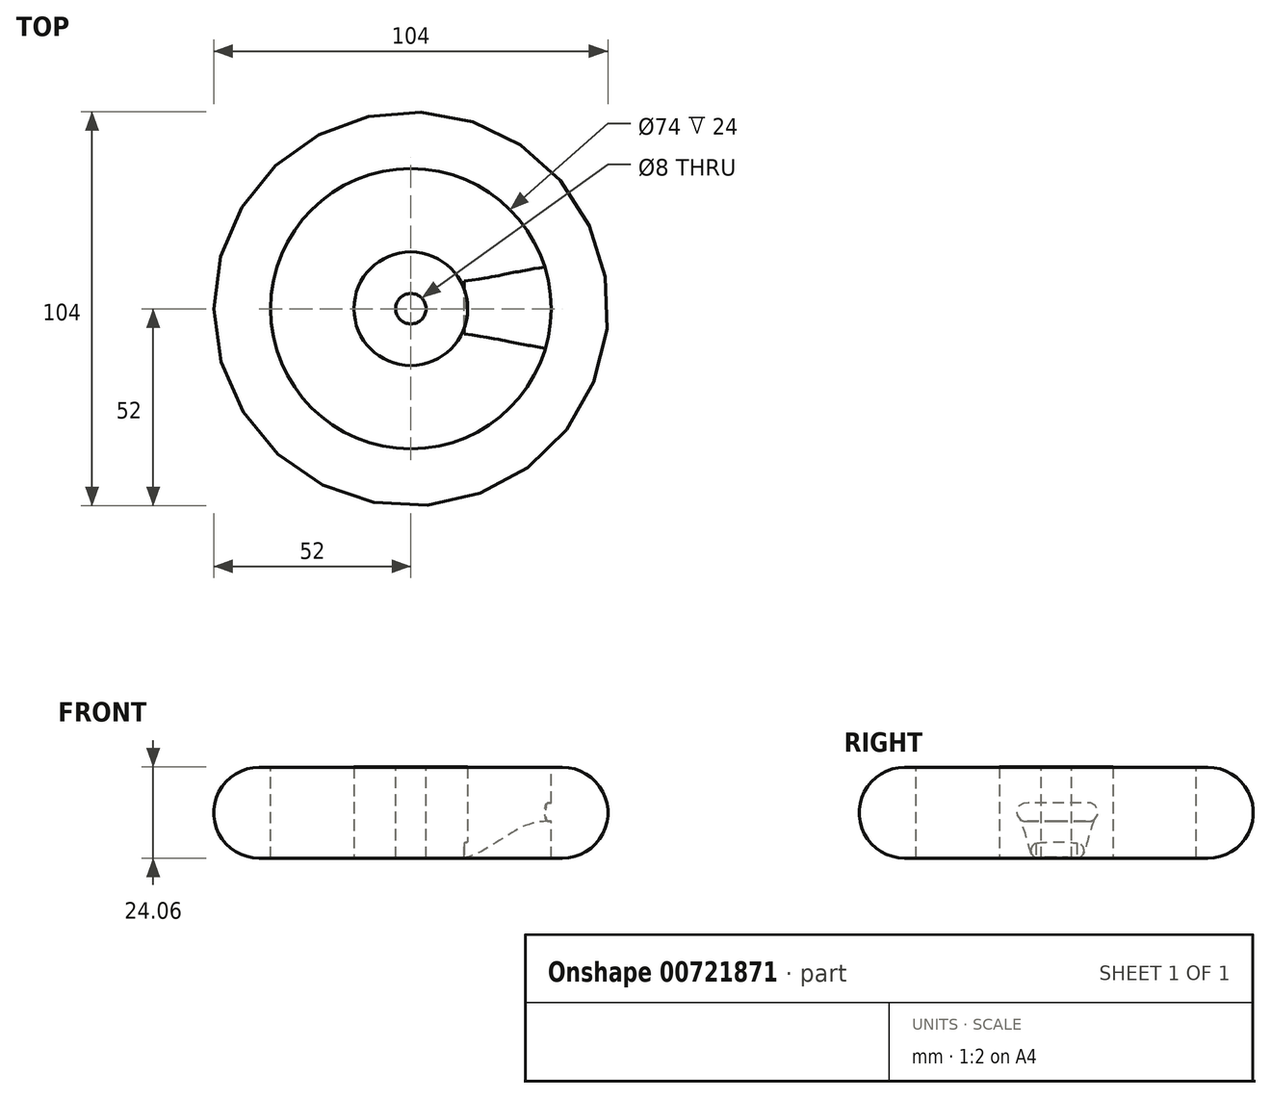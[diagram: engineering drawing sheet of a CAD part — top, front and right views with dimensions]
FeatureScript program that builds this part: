
annotation { "Feature Type Name" : "Feature", "Feature Type Description" : "" }
export const myFeature = defineFeature(function(context is Context, id is Id, definition is map)
    precondition{}
    {
        {
            var Q0;
            Q0=qCreatedBy(makeId("Top.planeOp"),FACE);
            var sketch = newSketch(context, id + "F0", { "sketchPlane" : qUnion([Q0])});
            skCircle(sketch, "E0", {"center": v(0, 0) * mm, "radius": 40 * mm});
            skSolve(sketch);
        }
        {
            var Q0;
            Q0=qCreatedBy(makeId("Front.planeOp"),FACE);
            var sketch = newSketch(context, id + "F1", { "sketchPlane" : qUnion([Q0])});
            skArc(sketch, "E1", {"start": v(-40, 12) * mm, "mid": v(-52, 0) * mm, "end": v(-40, -12) * mm});
            skLineSegment(sketch, "E2", {"start": v(-40, 12) * mm, "end": v(-37, 12) * mm});
            skLineSegment(sketch, "E3", {"start": v(-40, -12) * mm, "end": v(-37, -12) * mm});
            skLineSegment(sketch, "E4", {"start": v(-37, -12) * mm, "end": v(-37, 12) * mm});
            skSolve(sketch);
        }
        {
            var Q0;
            Q0=makeQuery(id+"F1.imprint","IMPRINT",FACE,{"disambiguationData":[TD([[makeQuery(id+"F1.imprint","IMPRINT",EDGE,{"derivedFrom":sQuery(id+"F1.wireOp",EDGE,"E1")}),1.0]])]});
            var Q1;
            Q1=sQuery(id+"F0.wireOp",EDGE,"E0");
            sweep(context, id + "F2", {"profiles" : qUnion([Q0]), "path" : qUnion([Q1])});
        }
        {
            var Q0;
            Q0=qCreatedBy(makeId("Right.planeOp"),FACE);
            cPlane(context, id + "F3", {"entities" : qUnion([Q0]), "cplaneType" : CPlaneType.OFFSET, "offset" : 40 * mm, "width" : 150 * mm, "height" : 150 * mm});
        }
        {
            var Q0;
            Q0=qCreatedBy(id+"F3.planeOp",FACE);
            var sketch = newSketch(context, id + "F4", { "sketchPlane" : qUnion([Q0])});
            skLineSegment(sketch, "E5", {"start": v(-8.69, 0) * mm, "end": v(9.31, 0) * mm});
            skArc(sketch, "E6.0.startCap", {"start": v(-8.69, -2.5) * mm, "mid": v(-11.19, 0) * mm, "end": v(-8.69, 2.5) * mm});
            skArc(sketch, "E6.0.endCap", {"start": v(9.31, 2.5) * mm, "mid": v(11.81, 0) * mm, "end": v(9.31, -2.5) * mm});
            skLineSegment(sketch, "E6.0.left", {"start": v(-8.69, 2.5) * mm, "end": v(9.31, 2.5) * mm});
            skLineSegment(sketch, "E6.0.right", {"start": v(-8.69, -2.5) * mm, "end": v(9.31, -2.5) * mm});
            skSolve(sketch);
        }
        {
            var Q0;
            Q0=qCreatedBy(makeId("Right.planeOp"),FACE);
            cPlane(context, id + "F5", {"entities" : qUnion([Q0]), "cplaneType" : CPlaneType.OFFSET, "offset" : 14 * mm, "width" : 150 * mm, "height" : 150 * mm});
        }
        {
            var Q0;
            Q0=qCreatedBy(id+"F5.planeOp",FACE);
            var sketch = newSketch(context, id + "F6", { "sketchPlane" : qUnion([Q0])});
            skLineSegment(sketch, "E7", {"start": v(-4.69, -10) * mm, "end": v(5.31, -10) * mm});
            skArc(sketch, "E8.0.startCap", {"start": v(-4.69, -12) * mm, "mid": v(-6.69, -10) * mm, "end": v(-4.69, -8) * mm});
            skArc(sketch, "E8.0.endCap", {"start": v(5.31, -8) * mm, "mid": v(7.31, -10) * mm, "end": v(5.31, -12) * mm});
            skLineSegment(sketch, "E8.0.left", {"start": v(-4.69, -8) * mm, "end": v(5.31, -8) * mm});
            skLineSegment(sketch, "E8.0.right", {"start": v(-4.69, -12) * mm, "end": v(5.31, -12) * mm});
            skSolve(sketch);
        }
        {
            var Q0;
            Q0=qCreatedBy(makeId("Front.planeOp"),FACE);
            var sketch = newSketch(context, id + "F7", { "sketchPlane" : qUnion([Q0])});
            skFitSpline(sketch, "E9", {"points": [v(14, -12) * mm, v(21.22, -8.7) * mm, v(25.51, -5.98) * mm, v(29.9, -3.56) * mm, v(34.75, -2.35) * mm, v(40, -2.5) * mm], "startDerivative": vector(34.97, 7.52) * mm, "endDerivative": vector(31.17, -2.37) * mm});
            skSolve(sketch);
        }
        {
            var Q1;
            Q1 = qSketchRegion(id + "F4", true);
            var Q2;
            Q2 = qSketchRegion(id + "F6", true);
            var Q3;
            Q3 = qConstructionFilter(qBodyType(qCreatedBy(id + "F7" ,EDGE), BodyType.WIRE), ConstructionObject.NO);
            loft(context, id + "F8", {"operationType" : NewBodyOperationType.ADD, "addGuides" : true, "sheetProfilesArray" : [{ "sheetProfileEntities" : qUnion([Q1]) }, { "sheetProfileEntities" : qUnion([Q2]) }], "guidesArray" : [{ "guideEntities" : qUnion([Q3]), "guideDerivativeType" : LoftGuideDerivativeType.DEFAULT, "guideDerivativeMagnitude" : 1 }]});
        }
        {
            var Q0;
            Q0=qCreatedBy(makeId("Front.planeOp"),FACE);
            var sketch = newSketch(context, id + "F9", { "sketchPlane" : qUnion([Q0])});
            skLineSegment(sketch, "E10.bottom", {"start": v(0, -11.94) * mm, "end": v(15, -11.94) * mm});
            skLineSegment(sketch, "E10.top", {"start": v(0, 12.06) * mm, "end": v(15, 12.06) * mm});
            skLineSegment(sketch, "E10.left", {"start": v(0, -11.94) * mm, "end": v(0, 12.06) * mm});
            skLineSegment(sketch, "E10.right", {"start": v(15, -11.94) * mm, "end": v(15, 12.06) * mm});
            skSolve(sketch);
        }
        {
            var Q0;
            Q0=makeQuery(id+"F9.imprint","IMPRINT",FACE,{"disambiguationData":[TD([[makeQuery(id+"F9.imprint","IMPRINT",EDGE,{"derivedFrom":sQuery(id+"F9.wireOp",EDGE,"E10.bottom")}),1.0]])]});
            var Q1;
            Q1=sQuery(id+"F9.wireOp",EDGE,"E10.left");
            revolve(context, id + "F10", {"operationType" : NewBodyOperationType.ADD, "surfaceOperationType" : NewSurfaceOperationType.NEW, "entities" : qUnion([Q0]), "axis" : qUnion([Q1]), "revolveType" : RevolveType.FULL});
        }
        {
            var Q0;
            Q0=makeQuery(id+"F10.opRevolve","SWEPT_FACE",FACE,{"disambiguationData":[OSD([sQuery(id+"F9.wireOp",EDGE,"E10.top")])]});
            var sketch = newSketch(context, id + "F11", { "sketchPlane" : qUnion([Q0])});
            skPoint(sketch, "E11", {"position": v(0, 0) * mm});
            skSolve(sketch);
        }
        {
            var Q0;
            Q0=sQuery(id+"F11.wireOp",VERTEX,"E11");
            var Q1;
            Q1=makeQuery(id+"F2.opSweep","SWEPT_BODY",BODY,{"disambiguationData":[OSD([sQuery(id+"F0.wireOp",EDGE,"E0"),sQuery(id+"F1.wireOp",EDGE,"E1"),sQuery(id+"F1.wireOp",EDGE,"E2"),sQuery(id+"F1.wireOp",EDGE,"E3"),sQuery(id+"F1.wireOp",EDGE,"E4")])]});
            hole(context, id + "F12", {"style" : HoleStyle.SIMPLE, "endStyle" : HoleEndStyle.BLIND, "holeDiameter" : 8 * mm, "majorDiameter" : 5 * mm, "holeDepth" : 50 * mm, "isTappedThrough" : true, "tappedDepth" : 12 * mm, "tapClearance" : 3, "locations" : qUnion([Q0]), "scope" : qUnion([Q1])});
        }
    });
